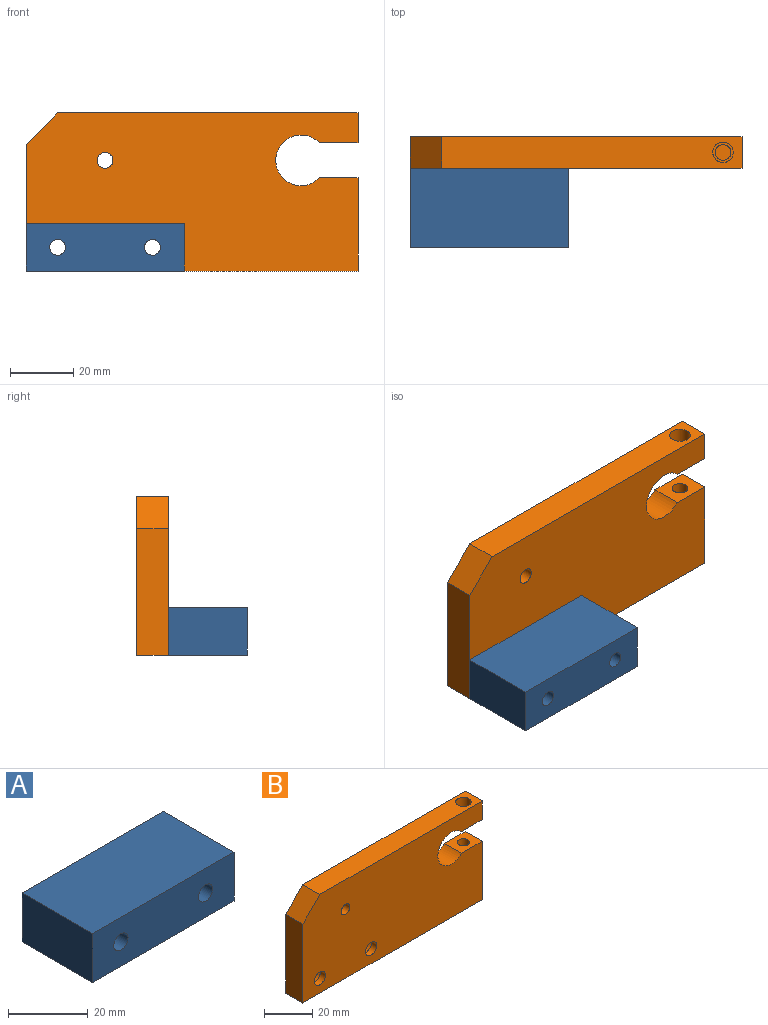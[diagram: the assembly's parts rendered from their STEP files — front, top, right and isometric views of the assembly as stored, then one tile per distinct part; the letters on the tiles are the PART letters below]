
ASSEMBLY  parts=2 mates=1
PART A: 8 faces, bbox 50x25x15 mm
  f0: plane 25x15mm, normal (-1,0,0), area 375mm2, adj f1,f5,f6,f7
  f1: plane 50x25mm, normal (0,0,-1), area 1250mm2, adj f0,f2,f6,f7
  f2: plane 25x15mm, normal (1,0,0), area 375mm2, adj f1,f5,f6,f7
  f3: cylinder r=2.5mm len=25mm, axis (0,1,0), area 392.7mm2, adj f6,f7
  f4: cylinder r=2.5mm len=25mm, axis (0,1,0), area 392.7mm2, adj f6,f7
  f5: plane 50x25mm, normal (0,0,1), area 1250mm2, adj f0,f2,f6,f7
  f6: plane 50x15mm, normal (0,-1,0), area 710.7mm2, adj f0,f1,f2,f3,f4,f5
  f7: plane 50x15mm, normal (0,1,0), area 710.7mm2, adj f0,f1,f2,f3,f4,f5
PART B: 21 faces, bbox 105x10x50 mm
  f0: cylinder r=3.25mm len=6.5mm, axis (0,1,0), area 61.3mm2, adj f11,f17
  f1: cylinder r=3.25mm len=6.5mm, axis (0,1,0), area 61.3mm2, adj f11,f15
  f2: cylinder r=8mm len=16mm, axis (0,1,0), area 381.4mm2, adj f3,f10,f11,f12
  f3: plane 12.19x10mm, normal (0,0,-1), area 88.7mm2, adj f2,f4,f11,f12,f18
  f4: plane 10x9.5mm, normal (1,0,0), area 95mm2, adj f3,f5,f11,f12
  f5: plane 95x10mm, normal (0,0,1), area 916.8mm2, adj f4,f11,f12,f13,f18
  f6: plane 40x10mm, normal (-1,0,0), area 400mm2, adj f7,f11,f12,f13
  f7: plane 105x10mm, normal (0,0,-1), area 1050mm2, adj f6,f8,f11,f12
  f8: plane 29.5x10mm, normal (1,0,0), area 295mm2, adj f7,f10,f11,f12
  f9: cylinder r=2.5mm len=10mm, axis (0,1,0), area 157.1mm2, adj f11,f12
  f10: plane 12.19x10mm, normal (0,0,1), area 102.3mm2, adj f2,f8,f11,f12,f19
  f11: plane 105x50mm, normal (0,-1,0), area 4795.4mm2, adj f0,f1,f2,f3,f4,f5,f6,f7
  f12: plane 105x50mm, normal (0,1,0), area 4671.7mm2, adj f2,f3,f4,f5,f6,f7,f8,f9
  f13: plane 10x10mm, normal (-0.71,0,0.71), area 141.4mm2, adj f5,f6,f11,f12
  f14: cylinder r=5.5mm len=11mm, axis (0,1,0), area 241.9mm2, adj f12,f15
  f15: plane 11x11mm, normal (0,1,0), area 61.9mm2, adj f1,f14
  f16: cylinder r=5.5mm len=11mm, axis (0,1,0), area 241.9mm2, adj f12,f17
  f17: plane 11x11mm, normal (0,1,0), area 61.9mm2, adj f0,f16
  f18: cylinder r=3.25mm len=9.5mm, axis (0,0,1), area 194mm2, adj f3,f5
  f19: cylinder r=2.5mm len=25.5mm, axis (0,0,1), area 400.6mm2, adj f10,f20
  f20: plane 5x5mm, normal (0,0,1), area 19.6mm2, adj f19
PLACE A t=(-3.41,-1.82,0.21)mm
PLACE B t=(24.09,20.68,17.71)mm
MATE fastened B.f0 <-> A.f3  axis (0,-1,0) through (-18.41,10.68,0.21)mm
